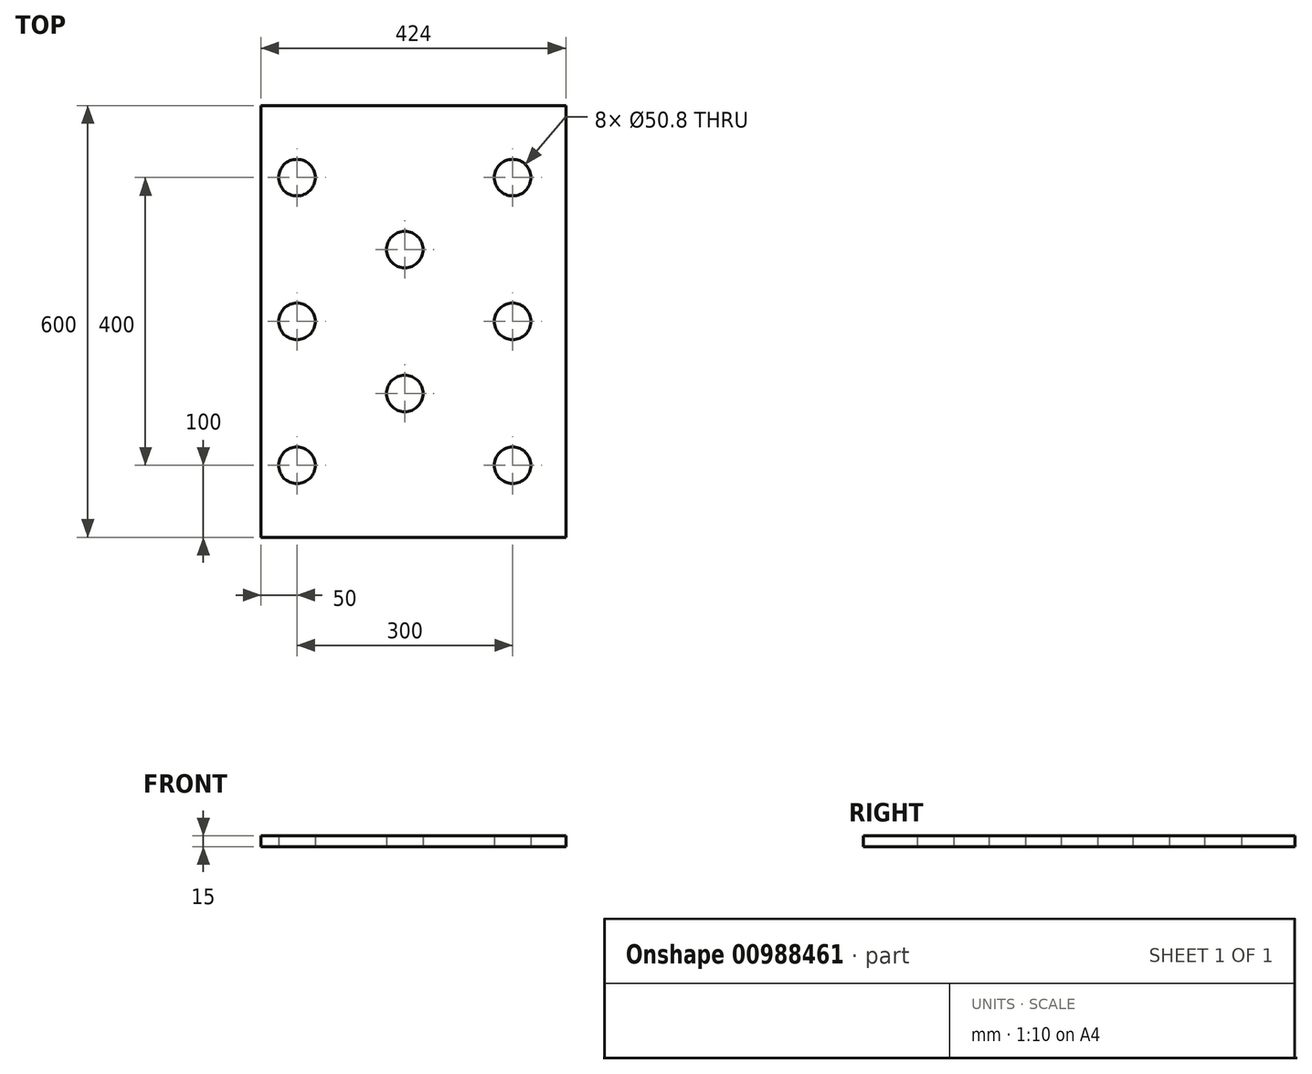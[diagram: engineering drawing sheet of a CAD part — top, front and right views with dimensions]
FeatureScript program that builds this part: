
annotation { "Feature Type Name" : "Feature", "Feature Type Description" : "" }
export const myFeature = defineFeature(function(context is Context, id is Id, definition is map)
    precondition{}
    {
        {
            var Q0;
            Q0=qCreatedBy(makeId("Top.planeOp"),FACE);
            var sketch = newSketch(context, id + "F0", { "sketchPlane" : qUnion([Q0])});
            skLineSegment(sketch, "E0.bottom", {"start": v(212, 300) * mm, "end": v(-212, 300) * mm});
            skLineSegment(sketch, "E0.top", {"start": v(212, -300) * mm, "end": v(-212, -300) * mm});
            skLineSegment(sketch, "E0.left", {"start": v(212, 300) * mm, "end": v(212, -300) * mm});
            skLineSegment(sketch, "E0.right", {"start": v(-212, 300) * mm, "end": v(-212, -300) * mm});
            skPoint(sketch, "E0.middle", {"position": v(0, 0) * mm});
            skLineSegment(sketch, "E1", {"start": v(-162, 300) * mm, "end": v(-162, -300) * mm, "construction": true});
            skLineSegment(sketch, "E2", {"start": v(138, 300) * mm, "end": v(138, -300) * mm, "construction": true});
            skLineSegment(sketch, "E3", {"start": v(-12, 300) * mm, "end": v(-12, -300) * mm, "construction": true});
            skPoint(sketch, "E4.0.1.0", {"position": v(-162, 0) * mm});
            skPoint(sketch, "E4.1.0.0", {"position": v(138, 200) * mm});
            skLineSegment(sketch, "E4.direction2", {"start": v(-162, 200) * mm, "end": v(-162, 0) * mm, "construction": true});
            skPoint(sketch, "E5", {"position": v(-162, 200) * mm});
            skPoint(sketch, "E6", {"position": v(138, 0) * mm});
            skPoint(sketch, "E7", {"position": v(-162, -200) * mm});
            skPoint(sketch, "E8", {"position": v(138, -200) * mm});
            skPoint(sketch, "E9", {"position": v(-12, 100) * mm});
            skPoint(sketch, "E10", {"position": v(-12, -100) * mm});
            skCircle(sketch, "E11", {"center": v(-162, 200) * mm, "radius": 25.4 * mm});
            skCircle(sketch, "E12", {"center": v(-162, 0) * mm, "radius": 25.4 * mm});
            skCircle(sketch, "E13", {"center": v(-162, -200) * mm, "radius": 25.4 * mm});
            skCircle(sketch, "E14", {"center": v(138, -200) * mm, "radius": 25.4 * mm});
            skCircle(sketch, "E15", {"center": v(138, 0) * mm, "radius": 25.4 * mm});
            skCircle(sketch, "E16", {"center": v(138, 200) * mm, "radius": 25.4 * mm});
            skCircle(sketch, "E17", {"center": v(-12, 100) * mm, "radius": 25.4 * mm});
            skCircle(sketch, "E18", {"center": v(-12, -100) * mm, "radius": 25.4 * mm});
            skSolve(sketch);
        }
        {
            var Q0;
            Q0=makeQuery(id+"F0.imprint","IMPRINT",FACE,{"disambiguationData":[TD([[makeQuery(id+"F0.imprint","IMPRINT",EDGE,{"derivedFrom":sQuery(id+"F0.wireOp",EDGE,"E0.bottom")}),1.0]])]});
            extrude(context, id + "F1", {"entities" : qUnion([Q0]), "depth" : 15 * mm, "offsetDistance" : 25 * mm});
        }
    });
